annotation { "Feature Type Name" : "Feature", "Feature Type Description" : "" }
export const myFeature = defineFeature(function(context is Context, id is Id, definition is map)
    precondition{}
    {
        {
            var Q0;
            Q0=qCreatedBy(makeId("Top.planeOp"),FACE);
            var sketch = newSketch(context, id + "F0", { "sketchPlane" : qUnion([Q0])});
            skLineSegment(sketch, "E0.rect.bottom", {"start": v(50, 7.07) * mm, "end": v(-50, 7.07) * mm});
            skLineSegment(sketch, "E0.rect.top", {"start": v(50, -7.07) * mm, "end": v(-50, -7.07) * mm});
            skLineSegment(sketch, "E0.rect.left", {"start": v(53.8, 3.26) * mm, "end": v(53.8, -3.26) * mm});
            skLineSegment(sketch, "E0.rect.right", {"start": v(-53.8, 3.26) * mm, "end": v(-53.8, -3.26) * mm});
            skPoint(sketch, "E0.rect.middle", {"position": v(0, 0) * mm});
            skPoint(sketch, "E1.visualSharp", {"position": v(-53.8, 7.07) * mm});
            skArc(sketch, "E1.filletArc", {"start": v(-50, 7.07) * mm, "mid": v(-52.69, 5.96) * mm, "end": v(-53.8, 3.26) * mm});
            skPoint(sketch, "E2.visualSharp", {"position": v(-53.8, -7.07) * mm});
            skArc(sketch, "E2.filletArc", {"start": v(-53.8, -3.26) * mm, "mid": v(-52.69, -5.96) * mm, "end": v(-50, -7.07) * mm});
            skPoint(sketch, "E3.visualSharp", {"position": v(53.8, 7.07) * mm});
            skArc(sketch, "E3.filletArc", {"start": v(53.8, 3.26) * mm, "mid": v(52.69, 5.96) * mm, "end": v(50, 7.07) * mm});
            skPoint(sketch, "E4.visualSharp", {"position": v(53.8, -7.07) * mm});
            skArc(sketch, "E4.filletArc", {"start": v(50, -7.07) * mm, "mid": v(52.69, -5.96) * mm, "end": v(53.8, -3.26) * mm});
            skCircle(sketch, "E5", {"center": v(-50.31, 0) * mm, "radius": 0.5 * mm});
            skCircle(sketch, "E6", {"center": v(50.5, 0) * mm, "radius": 0.5 * mm});
            skSolve(sketch);
        }
        {
            var Q0;
            Q0 = qSketchRegion(id + "F0", true);
            extrude(context, id + "F1", {"entities" : qUnion([Q0]), "oppositeDirection" : true, "depth" : 1.78 * mm});
        }
        {
            var Q0;
            Q0=qCreatedBy(makeId("Top.planeOp"),FACE);
            var sketch = newSketch(context, id + "F2", { "sketchPlane" : qUnion([Q0])});
            skText(sketch, "E7", { "text": "ALEXUS RAVERT", "fontName": "OpenSans-Bold.ttf"});
            const initialGuessF2  = {"E7": [-0.04188, -0.00402, 1, 0, 0.00777]};
            skSetInitialGuess(sketch, initialGuessF2);
            skSolve(sketch);
        }
        {
            var Q0;
            Q0 = qSketchRegion(id + "F2", true);
            extrude(context, id + "F3", {"entities" : qUnion([Q0]), "depth" : 1.78 * mm});
        }
    });